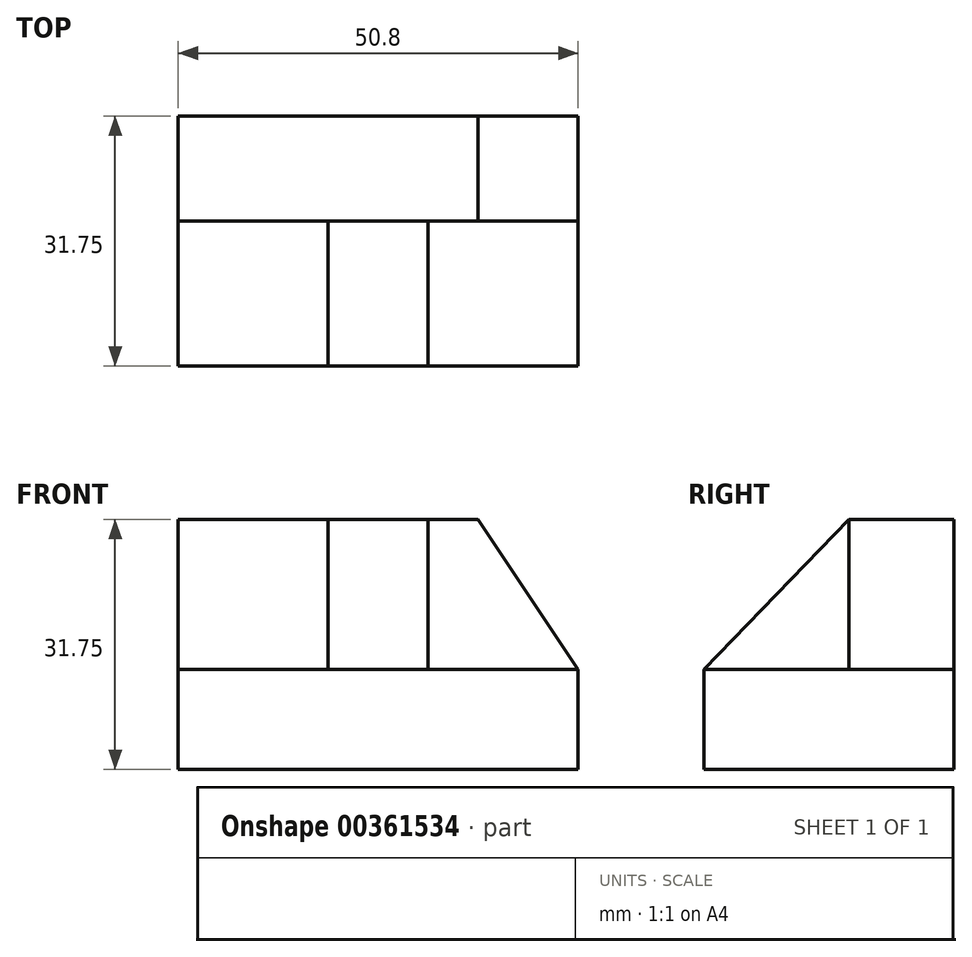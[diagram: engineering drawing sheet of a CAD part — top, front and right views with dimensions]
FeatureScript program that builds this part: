
annotation { "Feature Type Name" : "Feature", "Feature Type Description" : "" }
export const myFeature = defineFeature(function(context is Context, id is Id, definition is map)
    precondition{}
    {
        {
            var Q0;
            Q0=qCreatedBy(makeId("Top.planeOp"),FACE);
            var sketch = newSketch(context, id + "F0", { "sketchPlane" : qUnion([Q0])});
            skLineSegment(sketch, "E0", {"start": v(0, 31.75) * mm, "end": v(0, 0) * mm});
            skLineSegment(sketch, "E1", {"start": v(0, 0) * mm, "end": v(50.8, 0) * mm});
            skLineSegment(sketch, "E2", {"start": v(50.8, 0) * mm, "end": v(50.8, 31.75) * mm});
            skLineSegment(sketch, "E3", {"start": v(50.8, 31.75) * mm, "end": v(0, 31.75) * mm});
            skSolve(sketch);
        }
        {
            var Q0;
            Q0 = qSketchRegion(id + "F0", true);
            extrude(context, id + "F1", {"entities" : qUnion([Q0]), "depth" : 12.7 * mm});
        }
        {
            var Q0;
            Q0=makeQuery(id+"F1.opExtrude","CAP_FACE",FACE,{"disambiguationData":[OSD([sQuery(id+"F0.wireOp",EDGE,"E0"),sQuery(id+"F0.wireOp",EDGE,"E1"),sQuery(id+"F0.wireOp",EDGE,"E2"),sQuery(id+"F0.wireOp",EDGE,"E3")])],"isStart":false});
            var sketch = newSketch(context, id + "F2", { "sketchPlane" : qUnion([Q0])});
            skLineSegment(sketch, "E4", {"start": v(0, 18.42) * mm, "end": v(50.8, 18.42) * mm});
            skLineSegment(sketch, "E5", {"start": v(50.8, 18.42) * mm, "end": v(50.8, 31.75) * mm});
            skLineSegment(sketch, "E6", {"start": v(50.8, 31.75) * mm, "end": v(0, 31.75) * mm});
            skLineSegment(sketch, "E7", {"start": v(0, 31.75) * mm, "end": v(0, 18.42) * mm});
            skSolve(sketch);
        }
        {
            var Q0;
            Q0=makeQuery(id+"F2.imprint","IMPRINT",FACE,{"disambiguationData":[TD([[makeQuery(id+"F2.imprint","IMPRINT",EDGE,{"derivedFrom":sQuery(id+"F2.wireOp",EDGE,"E4")}),1.0]])]});
            extrude(context, id + "F3", {"entities" : qUnion([Q0]), "operationType" : NewBodyOperationType.ADD, "depth" : 19.05 * mm});
        }
        {
            var Q0;
            Q0=makeQuery(id+"F3.opExtrude","SWEPT_FACE",FACE,{"disambiguationData":[OSD([sQuery(id+"F2.wireOp",EDGE,"E4")])]});
            var sketch = newSketch(context, id + "F4", { "sketchPlane" : qUnion([Q0])});
            skLineSegment(sketch, "E8", {"start": v(50.8, 12.7) * mm, "end": v(38.1, 31.75) * mm});
            skLineSegment(sketch, "E9", {"start": v(38.1, 31.75) * mm, "end": v(50.8, 31.75) * mm});
            skLineSegment(sketch, "E10", {"start": v(50.8, 31.75) * mm, "end": v(50.8, 12.7) * mm});
            skSolve(sketch);
        }
        {
            var Q0;
            Q0=makeQuery(id+"F4.imprint","IMPRINT",FACE,{"disambiguationData":[TD([[makeQuery(id+"F4.imprint","IMPRINT",EDGE,{"derivedFrom":sQuery(id+"F4.wireOp",EDGE,"E8")}),-1.0]])]});
            extrude(context, id + "F5", {"entities" : qUnion([Q0]), "operationType" : NewBodyOperationType.REMOVE, "oppositeDirection" : true, "depth" : 25.4 * mm});
        }
        {
            var Q0;
            Q0=makeQuery(id+"F1.opExtrude","CAP_FACE",FACE,{"disambiguationData":[OSD([sQuery(id+"F0.wireOp",EDGE,"E0"),sQuery(id+"F0.wireOp",EDGE,"E1"),sQuery(id+"F0.wireOp",EDGE,"E2"),sQuery(id+"F0.wireOp",EDGE,"E3")])],"isStart":false});
            var sketch = newSketch(context, id + "F6", { "sketchPlane" : qUnion([Q0])});
            skSolve(sketch);
        }
        {
            var Q0;
            Q0=makeQuery(id+"F6.imprint","IMPRINT",FACE,{"disambiguationData":[TD([[makeQuery(id+"F6.imprint","IMPRINT",EDGE,{"derivedFrom":makeQuery(id+"F1.opExtrude","CAP_EDGE",EDGE,{"disambiguationData":[OSD([sQuery(id+"F0.wireOp",EDGE,"E1")])],"isStart":false})}),1.0]])]});
            var sketch = newSketch(context, id + "F7", { "sketchPlane" : qUnion([Q0])});
            skLineSegment(sketch, "E11", {"start": v(19.05, 19.05) * mm, "end": v(19.05, 0) * mm});
            skLineSegment(sketch, "E12", {"start": v(19.05, 0) * mm, "end": v(31.75, 0) * mm});
            skLineSegment(sketch, "E13", {"start": v(19.05, 19.05) * mm, "end": v(31.75, 19.05) * mm});
            skLineSegment(sketch, "E14", {"start": v(31.75, 19.05) * mm, "end": v(31.75, 0) * mm});
            skSolve(sketch);
        }
        {
            var Q0;
            Q0 = qSketchRegion(id + "F7", true);
            extrude(context, id + "F8", {"entities" : qUnion([Q0]), "operationType" : NewBodyOperationType.ADD, "depth" : 19.05 * mm});
        }
        {
            var Q0;
            Q0=makeQuery(id+"F8.opExtrude","SWEPT_FACE",FACE,{"disambiguationData":[OSD([sQuery(id+"F7.wireOp",EDGE,"E14")])]});
            var sketch = newSketch(context, id + "F9", { "sketchPlane" : qUnion([Q0])});
            skLineSegment(sketch, "E15", {"start": v(18.42, 31.75) * mm, "end": v(0, 12.7) * mm});
            skLineSegment(sketch, "E16", {"start": v(0, 12.7) * mm, "end": v(0, 31.75) * mm});
            skLineSegment(sketch, "E17", {"start": v(0, 31.75) * mm, "end": v(18.42, 31.75) * mm});
            skSolve(sketch);
        }
        {
            var Q0;
            Q0=makeQuery(id+"F9.imprint","IMPRINT",FACE,{"disambiguationData":[TD([[makeQuery(id+"F9.imprint","IMPRINT",EDGE,{"derivedFrom":sQuery(id+"F9.wireOp",EDGE,"E15")}),-1.0]])]});
            extrude(context, id + "F10", {"entities" : qUnion([Q0]), "operationType" : NewBodyOperationType.REMOVE, "oppositeDirection" : true, "depth" : 19.05 * mm});
        }
    });
